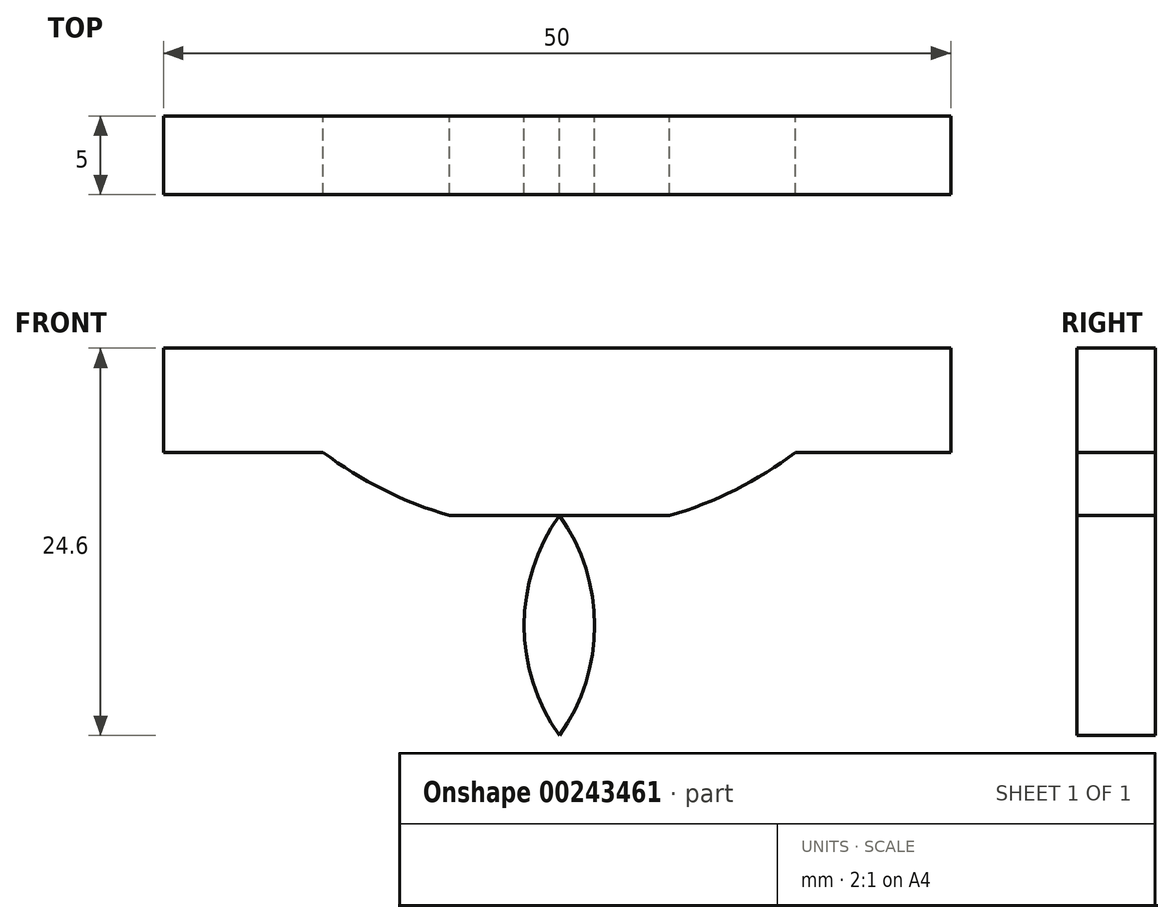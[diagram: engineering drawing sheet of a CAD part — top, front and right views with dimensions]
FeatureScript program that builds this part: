
annotation { "Feature Type Name" : "Feature", "Feature Type Description" : "" }
export const myFeature = defineFeature(function(context is Context, id is Id, definition is map)
    precondition{}
    {
        {
            var Q0;
            Q0=qCreatedBy(makeId("Front.planeOp"),FACE);
            var sketch = newSketch(context, id + "F0", { "sketchPlane" : qUnion([Q0])});
            skLineSegment(sketch, "E0", {"start": v(-17.47, 39.8) * mm, "end": v(32.53, 39.8) * mm});
            skLineSegment(sketch, "E1", {"start": v(32.53, 39.8) * mm, "end": v(32.53, 33.18) * mm});
            skLineSegment(sketch, "E2", {"start": v(32.53, 33.18) * mm, "end": v(-17.47, 33.18) * mm});
            skLineSegment(sketch, "E3", {"start": v(-17.47, 33.18) * mm, "end": v(-17.47, 39.8) * mm});
            skArc(sketch, "E4", {"start": v(-7.33, 33.18) * mm, "mid": v(-3.5, 30.81) * mm, "end": v(0.68, 29.17) * mm});
            skLineSegment(sketch, "E5", {"start": v(14.67, 29.17) * mm, "end": v(0.68, 29.17) * mm});
            skArc(sketch, "E6.trimOffspring", {"start": v(14.67, 29.17) * mm, "mid": v(18.85, 30.81) * mm, "end": v(22.67, 33.18) * mm});
            skArc(sketch, "E7", {"start": v(7.67, 29.17) * mm, "mid": v(5.43, 22.2) * mm, "end": v(7.67, 15.2) * mm});
            skPoint(sketch, "E7.endSnap0", {"position": v(7.67, 29.17) * mm});
            skArc(sketch, "E8", {"start": v(7.67, 15.2) * mm, "mid": v(9.91, 22.2) * mm, "end": v(7.67, 29.17) * mm});
            skArc(sketch, "E9", {"start": v(0.68, 29.17) * mm, "mid": v(0.52, 24.1) * mm, "end": v(5.6, 24.22) * mm});
            skArc(sketch, "E10", {"start": v(9.74, 24.22) * mm, "mid": v(15, 23.9) * mm, "end": v(14.67, 29.17) * mm});
            skSolve(sketch);
        }
        {
            var Q0;
            Q0 = qSketchRegion(id + "F0", true);
            extrude(context, id + "F1", {"entities" : qUnion([Q0]), "depth" : 5 * mm, "offsetDistance" : 25 * mm});
        }
        {
            var Q0;
            Q0=makeQuery(id+"F1.opExtrude","CAP_FACE",FACE,{"disambiguationData":[OSD([sQuery(id+"F0.wireOp",EDGE,"E0"),sQuery(id+"F0.wireOp",EDGE,"E1"),sQuery(id+"F0.wireOp",EDGE,"E2"),sQuery(id+"F0.wireOp",EDGE,"E3"),sQuery(id+"F0.wireOp",EDGE,"E4"),sQuery(id+"F0.wireOp",EDGE,"E6.trimOffspring"),sQuery(id+"F0.wireOp",EDGE,"E7"),sQuery(id+"F0.wireOp",EDGE,"E8"),sQuery(id+"F0.wireOp",EDGE,"E9"),sQuery(id+"F0.wireOp",EDGE,"E10")])],"isStart":false});
            var Q1;
            Q1=makeQuery(id+"F1.opExtrude","SWEPT_BODY",BODY,{"disambiguationData":[OSD([sQuery(id+"F0.wireOp",EDGE,"E0"),sQuery(id+"F0.wireOp",EDGE,"E1"),sQuery(id+"F0.wireOp",EDGE,"E2"),sQuery(id+"F0.wireOp",EDGE,"E3"),sQuery(id+"F0.wireOp",EDGE,"E4"),sQuery(id+"F0.wireOp",EDGE,"E6.trimOffspring"),sQuery(id+"F0.wireOp",EDGE,"E7"),sQuery(id+"F0.wireOp",EDGE,"E8"),sQuery(id+"F0.wireOp",EDGE,"E9"),sQuery(id+"F0.wireOp",EDGE,"E10")])]});
            shell(context, id + "F2", {"isHollow" : true, "entities" : qUnion([Q0]), "parts" : qUnion([Q1]), "thickness" : 2.5 * mm});
        }
    });
